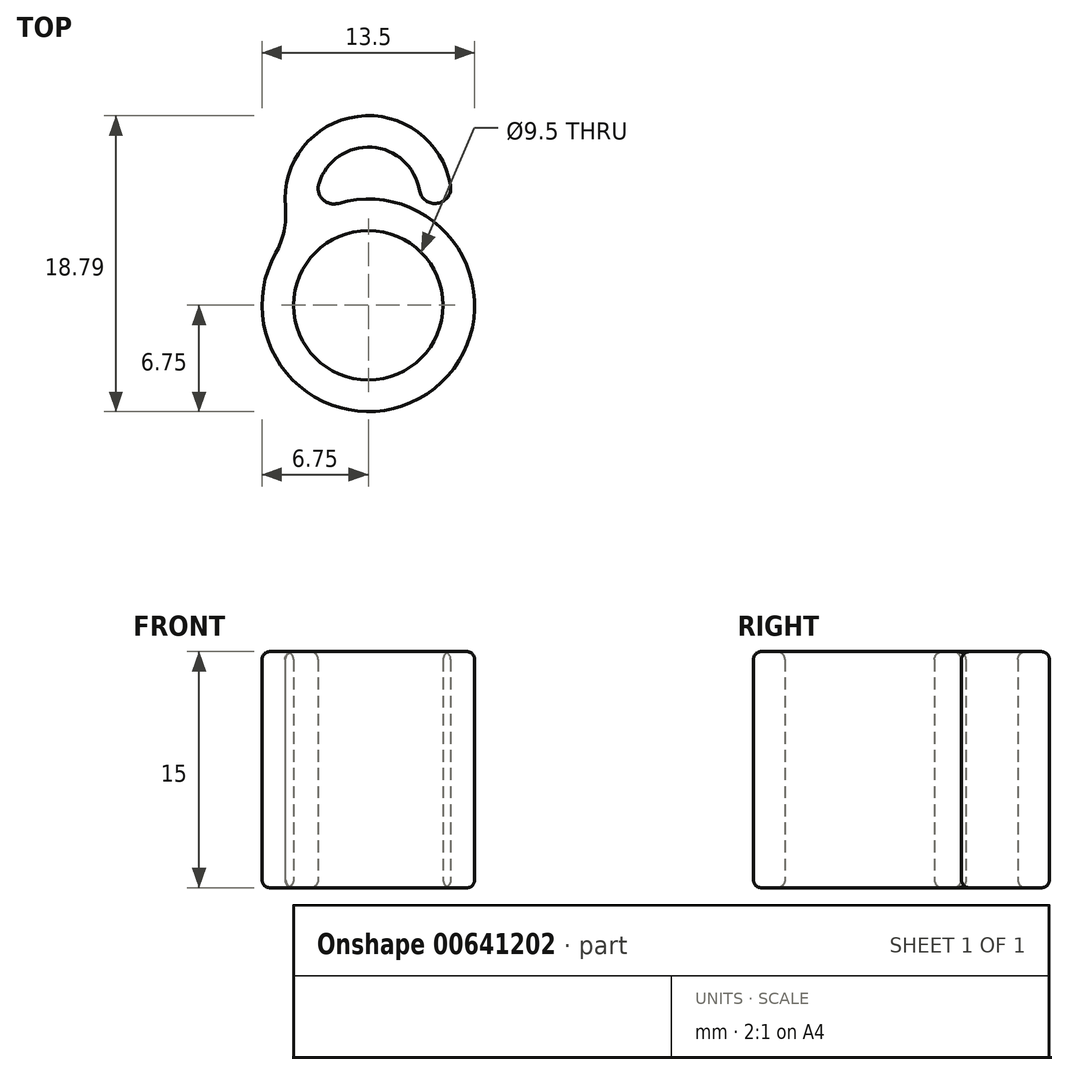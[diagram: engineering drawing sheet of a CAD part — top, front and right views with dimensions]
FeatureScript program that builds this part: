
annotation { "Feature Type Name" : "Feature", "Feature Type Description" : "" }
export const myFeature = defineFeature(function(context is Context, id is Id, definition is map)
    precondition{}
    {
        {
            var Q0;
            Q0=qCreatedBy(makeId("Top.planeOp"),FACE);
            var sketch = newSketch(context, id + "F0", { "sketchPlane" : qUnion([Q0])});
            skCircle(sketch, "E0", {"center": v(0, 0) * mm, "radius": 4.75 * mm});
            skCircle(sketch, "E1.0", {"center": v(0, 0) * mm, "radius": 6.75 * mm});
            skLineSegment(sketch, "E2", {"start": v(0, 0) * mm, "end": v(0, 10.8) * mm, "construction": true});
            skCircle(sketch, "E3", {"center": v(0, 6.75) * mm, "radius": 5.3 * mm});
            skCircle(sketch, "E4", {"center": v(0, 6.75) * mm, "radius": 3.3 * mm});
            skLineSegment(sketch, "E5", {"start": v(3.3, 6.89) * mm, "end": v(5.18, 5.65) * mm});
            skSolve(sketch);
        }
        {
            var Q0;
            {var subQ0=sQuery(id+"F0.wireOp",EDGE,"E3");var subQ1=sQuery(id+"F0.wireOp",EDGE,"E0");var subQ2=makeQuery(id+"F0.imprint","INTERSECT",VERTEX,{"disambiguationData":[OD(0.0)],"derivedFrom":[subQ1,subQ0]});Q0=makeQuery(id+"F0.imprint","IMPRINT",FACE,{"disambiguationData":[TD([[makeQuery(id+"F0.imprint","IMPRINT",EDGE,{"disambiguationData":[TD([[subQ2,1.0]])],"derivedFrom":subQ1}),-1.0]])]});}
            var Q1;
            {var subQ0=sQuery(id+"F0.wireOp",EDGE,"E4");var subQ1=sQuery(id+"F0.wireOp",EDGE,"E0");var subQ2=makeQuery(id+"F0.imprint","INTERSECT",VERTEX,{"disambiguationData":[OD(1.0)],"derivedFrom":[subQ1,subQ0]});Q1=makeQuery(id+"F0.imprint","IMPRINT",FACE,{"disambiguationData":[TD([[makeQuery(id+"F0.imprint","IMPRINT",EDGE,{"disambiguationData":[TD([[subQ2,-1.0]])],"derivedFrom":subQ1}),-1.0]])]});}
            var Q2;
            {var subQ0=sQuery(id+"F0.wireOp",EDGE,"E4");var subQ1=sQuery(id+"F0.wireOp",EDGE,"E0");var subQ2=makeQuery(id+"F0.imprint","INTERSECT",VERTEX,{"disambiguationData":[OD(0.0)],"derivedFrom":[subQ1,subQ0]});Q2=makeQuery(id+"F0.imprint","IMPRINT",FACE,{"disambiguationData":[TD([[makeQuery(id+"F0.imprint","IMPRINT",EDGE,{"disambiguationData":[TD([[subQ2,-1.0]])],"derivedFrom":subQ1}),-1.0]])]});}
            var Q3;
            {var subQ0=sQuery(id+"F0.wireOp",EDGE,"E4");var subQ1=sQuery(id+"F0.wireOp",EDGE,"E0");var subQ2=makeQuery(id+"F0.imprint","INTERSECT",VERTEX,{"disambiguationData":[OD(0.0)],"derivedFrom":[subQ1,subQ0]});Q3=makeQuery(id+"F0.imprint","IMPRINT",FACE,{"disambiguationData":[TD([[makeQuery(id+"F0.imprint","IMPRINT",EDGE,{"disambiguationData":[TD([[subQ2,1.0]])],"derivedFrom":subQ1}),-1.0]])]});}
            var Q4;
            {var subQ5=sQuery(id+"F0.wireOp",EDGE,"E5");Q4=makeQuery(id+"F0.imprint","IMPRINT",FACE,{"disambiguationData":[TD([[makeQuery(id+"F0.imprint","IMPRINT",EDGE,{"derivedFrom":subQ5}),1.0]])]});}
            extrude(context, id + "F1", {"entities" : qUnion([Q0, Q1, Q2, Q3, Q4]), "depth" : 15 * mm, "offsetDistance" : 25 * mm});
        }
        {
            var Q0;
            Q0=makeQuery(id+"F1.opExtrude","SWEPT_EDGE",EDGE,{"disambiguationData":[OSD([sQuery(id+"F0.wireOp",EDGE,"E1.0"),sQuery(id+"F0.wireOp",EDGE,"E3")])]});
            fillet(context, id + "F2", {"entities" : qUnion([Q0]), "radius" : 5 * mm, "tangentPropagation" : true, "allowEdgeOverflow" : false});
        }
        {
            var Q0;
            Q0=makeQuery(id+"F1.opExtrude","SWEPT_EDGE",EDGE,{"disambiguationData":[OSD([sQuery(id+"F0.wireOp",EDGE,"E3"),sQuery(id+"F0.wireOp",EDGE,"E5")])]});
            var Q1;
            Q1=makeQuery(id+"F1.opExtrude","SWEPT_EDGE",EDGE,{"disambiguationData":[OSD([sQuery(id+"F0.wireOp",EDGE,"E4"),sQuery(id+"F0.wireOp",EDGE,"E5")])]});
            var Q2;
            Q2=makeQuery(id+"F1.opExtrude","SWEPT_EDGE",EDGE,{"disambiguationData":[OSD([sQuery(id+"F0.wireOp",EDGE,"E1.0"),sQuery(id+"F0.wireOp",EDGE,"E4")])]});
            fillet(context, id + "F3", {"entities" : qUnion([Q0, Q1, Q2]), "radius" : 1 * mm, "tangentPropagation" : true, "allowEdgeOverflow" : false});
        }
        {
            var Q0;
            Q0=makeQuery(id+"F1.opExtrude","CAP_EDGE",EDGE,{"disambiguationData":[OSD([sQuery(id+"F0.wireOp",EDGE,"E3")])],"isStart":false});
            var Q1;
            Q1=makeQuery(id+"F1.opExtrude","CAP_EDGE",EDGE,{"disambiguationData":[OSD([sQuery(id+"F0.wireOp",EDGE,"E0")])],"isStart":false});
            var Q2;
            Q2=makeQuery(id+"F1.opExtrude","CAP_EDGE",EDGE,{"disambiguationData":[OSD([sQuery(id+"F0.wireOp",EDGE,"E4")])],"isStart":true});
            var Q3;
            Q3=makeQuery(id+"F1.opExtrude","CAP_EDGE",EDGE,{"disambiguationData":[OSD([sQuery(id+"F0.wireOp",EDGE,"E0")])],"isStart":true});
            fillet(context, id + "F4", {"entities" : qUnion([Q0, Q1, Q2, Q3]), "radius" : 0.5 * mm, "tangentPropagation" : true, "allowEdgeOverflow" : false});
        }
    });
